# Revit family: HTVZDSS-WF
name_source: partatom
category: Plumbing Fixtures
units: mm (PartAtom-declared; Revit-internal decimal feet)

## family parameters
Always vertical = Yes
Cut with Voids When Loaded = No
OmniClass Number = 23.45.00.00
OmniClass Title = Sanitary, Laundry, and Cleaning Equipment
Part Type = Normal
Room Calculation Point = No
Round Connector Dimension = Use Radius
Shared = No
Work Plane-Based = No

## types (8) — shared parameters
Activation = Pushbars
Basin Material = Metal - Steel - Stainless - Chrome
Bubbler = Double Bubbler
CW Connection = Yes
Cooler Bottom = 1' - 0 1/2"
Cooler Depth = 1' - 7"
Cooler Height = 1' - 8 3/8"
Cooler Rear Panel Depth = 0' - 6 43/256"
Cooler Separation = 0' - 0"
Cooler Width = 1' - 6 57/64"
Description = Voyager HTVZ
Dispenser ADA Height = 2' - 4 19/32"
Dispenser Depth = 0' - 8 25/64"
Floor to Bottom = 1' - 0 1/2"
HW Connection = No
Louver Screens = -
Manufacturer = Halsey Taylor
Orifice Height = 2' - 8 7/8"
Orifice to Rim = 0' - 1 9/16"
Panel Material = Metal - Steel - Stainless - Color 3
Rim Height = 2' - 7 5/16"
Rim to Dispenser = 0' - 4 9/32"
Rim to Top of Bottom Panel = 0' - 5 9/32"
Specification = http://www.halseytaylor.com
TOP SKETCH = Yes
Top Panel Material = Metal - Steel - Stainless - Color 2
Type = Single
URL = http://www.halseytaylor.com
Vent Connection = No
Version = 1.0.0.0
Volts/Hertz = 115V/60Hz
Waste Connection = Yes
Water Service Flow = 0 GPM
Water Service Size Radius = 0' - 0 1/4"

## per-type parameters (varying)
| type | Filter | Refrigerated |
| HTVZ8PV-NF |  | Yes |
| HTVZ8PV-WF | HWF172 | Yes |
| HTVZ8SS-NF |  | Yes |
| HTVZ8SS-WS |  | Yes |
| HTVZDPV-NF |  | No |
| HTVZDPV-WF | HWF172 | No |
| HTVZDSS-NF |  | No |
| HTVZDSS-WF | HWF172 | No |

note: column(s) folded — value = type name in every type: Model

## geometry (parser evidence)
native form markers: Extrusion x1, Sweep x7
no freeform markers — native parametric forms only
